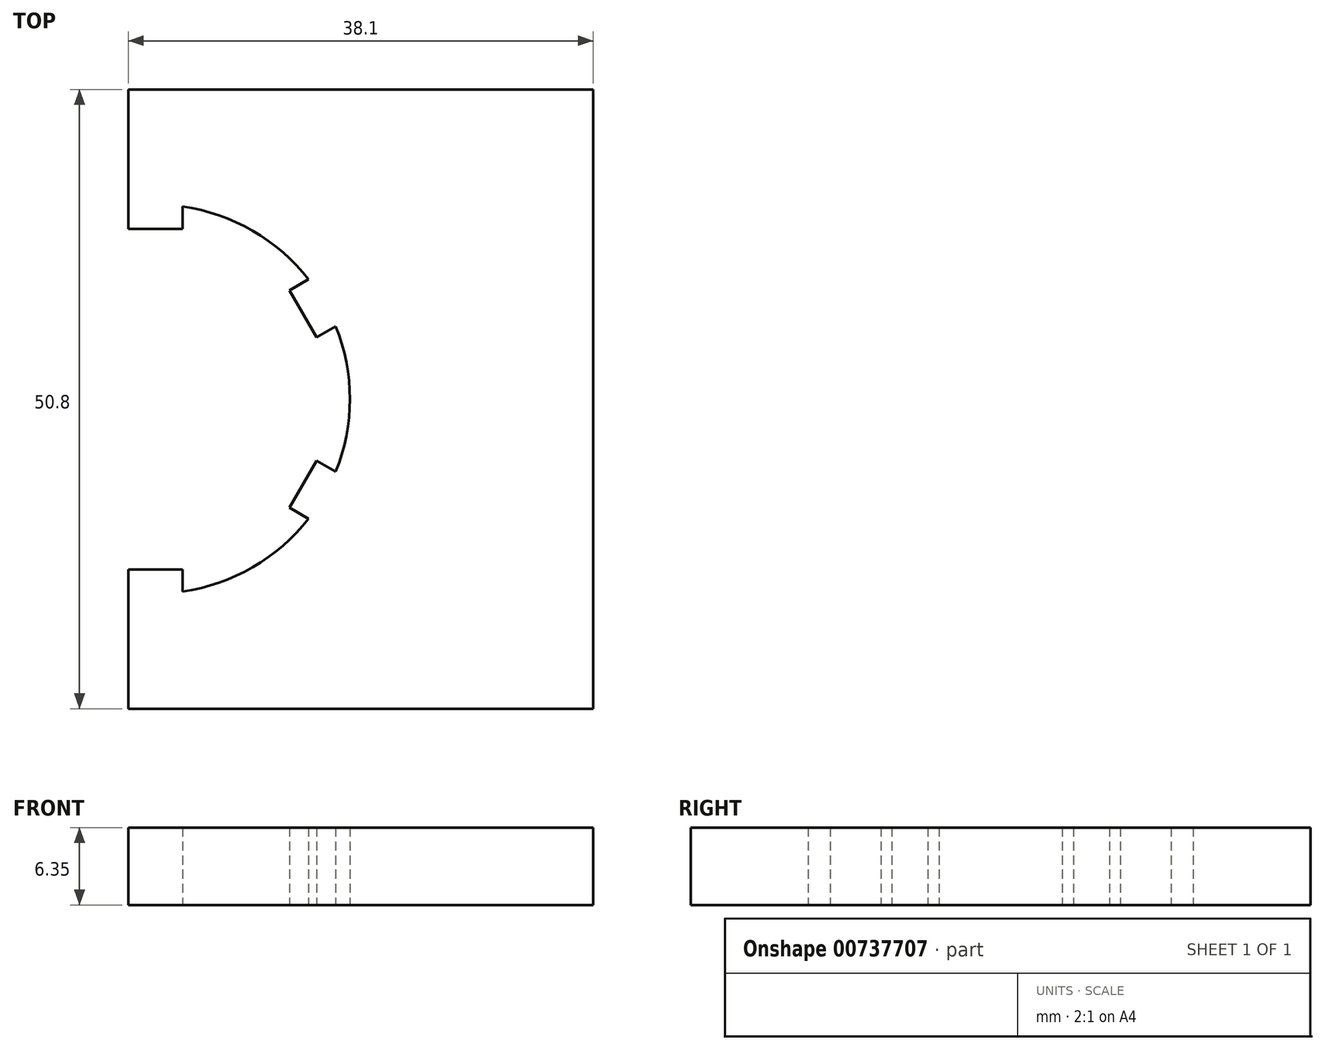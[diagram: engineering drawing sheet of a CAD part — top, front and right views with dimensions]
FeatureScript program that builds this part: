
annotation { "Feature Type Name" : "Feature", "Feature Type Description" : "" }
export const myFeature = defineFeature(function(context is Context, id is Id, definition is map)
    precondition{}
    {
        {
            var Q0;
            Q0=qCreatedBy(makeId("Top.planeOp"),FACE);
            var sketch = newSketch(context, id + "F0", { "sketchPlane" : qUnion([Q0])});
            skCircle(sketch, "E0", {"center": v(0, 0) * mm, "radius": 15.94 * mm, "construction": true});
            skLineSegment(sketch, "E1", {"start": v(0, 0) * mm, "end": v(0, 21.25) * mm});
            skLineSegment(sketch, "E2.0", {"start": v(2.22, 13.97) * mm, "end": v(2.22, 15.78) * mm, "construction": true});
            skLineSegment(sketch, "E3.0", {"start": v(-2.22, 13.97) * mm, "end": v(-2.22, 15.78) * mm, "construction": true});
            skLineSegment(sketch, "E4", {"start": v(-2.22, 13.97) * mm, "end": v(2.22, 13.97) * mm, "construction": true});
            skLineSegment(sketch, "E5", {"start": v(-20.95, 0) * mm, "end": v(26.76, 0) * mm, "construction": true});
            skPoint(sketch, "E6.orphan", {"position": v(-2.22, 0) * mm});
            skPoint(sketch, "E7.MirrorCS.end.orphan", {"position": v(2.22, 13.97) * mm});
            skPoint(sketch, "E7.MirrorCS.start.orphan", {"position": v(6.67, 13.97) * mm});
            skLineSegment(sketch, "E8.1.0", {"start": v(-13.2, 5.06) * mm, "end": v(-14.78, 5.97) * mm, "construction": true});
            skLineSegment(sketch, "E8.1.1", {"start": v(-13.2, 5.06) * mm, "end": v(-10.99, 8.9) * mm, "construction": true});
            skLineSegment(sketch, "E8.1.2", {"start": v(-10.99, 8.9) * mm, "end": v(-12.56, 9.82) * mm, "construction": true});
            skLineSegment(sketch, "E8.2.0", {"start": v(-10.99, -8.9) * mm, "end": v(-12.56, -9.82) * mm, "construction": true});
            skLineSegment(sketch, "E8.2.1", {"start": v(-10.99, -8.9) * mm, "end": v(-13.2, -5.06) * mm, "construction": true});
            skLineSegment(sketch, "E8.2.2", {"start": v(-13.2, -5.06) * mm, "end": v(-14.78, -5.97) * mm, "construction": true});
            skLineSegment(sketch, "E8.3.0", {"start": v(2.22, -13.97) * mm, "end": v(2.22, -15.78) * mm, "construction": true});
            skLineSegment(sketch, "E8.3.1", {"start": v(2.22, -13.97) * mm, "end": v(-2.22, -13.97) * mm, "construction": true});
            skLineSegment(sketch, "E8.3.2", {"start": v(-2.22, -13.97) * mm, "end": v(-2.22, -15.78) * mm, "construction": true});
            skLineSegment(sketch, "E8.4.0", {"start": v(13.2, -5.06) * mm, "end": v(14.78, -5.97) * mm, "construction": true});
            skLineSegment(sketch, "E8.4.1", {"start": v(13.2, -5.06) * mm, "end": v(10.99, -8.9) * mm, "construction": true});
            skLineSegment(sketch, "E8.4.2", {"start": v(10.99, -8.9) * mm, "end": v(12.56, -9.82) * mm, "construction": true});
            skLineSegment(sketch, "E8.5.0", {"start": v(10.99, 8.9) * mm, "end": v(12.56, 9.82) * mm, "construction": true});
            skLineSegment(sketch, "E8.5.1", {"start": v(10.99, 8.9) * mm, "end": v(13.2, 5.06) * mm, "construction": true});
            skLineSegment(sketch, "E8.5.2", {"start": v(13.2, 5.06) * mm, "end": v(14.78, 5.97) * mm, "construction": true});
            skSolve(sketch);
        }
        {
            var Q0;
            Q0=qCreatedBy(makeId("Top.planeOp"),FACE);
            var sketch = newSketch(context, id + "F1", { "sketchPlane" : qUnion([Q0])});
            skLineSegment(sketch, "E9.0", {"start": v(-2.22, 13.97) * mm, "end": v(2.22, 13.97) * mm});
            skLineSegment(sketch, "E10.0", {"start": v(2.22, 13.97) * mm, "end": v(2.22, 15.78) * mm});
            skLineSegment(sketch, "E11.0", {"start": v(-2.22, 13.97) * mm, "end": v(-2.22, 15.78) * mm});
            skPoint(sketch, "E12.0", {"position": v(11.77, 9.36) * mm});
            skLineSegment(sketch, "E13.0", {"start": v(10.99, 8.9) * mm, "end": v(12.56, 9.82) * mm});
            skLineSegment(sketch, "E14.0", {"start": v(10.99, 8.9) * mm, "end": v(13.2, 5.06) * mm});
            skLineSegment(sketch, "E15.0", {"start": v(13.2, 5.06) * mm, "end": v(14.78, 5.97) * mm});
            skLineSegment(sketch, "E16.0", {"start": v(13.2, -5.06) * mm, "end": v(10.99, -8.9) * mm});
            skLineSegment(sketch, "E17.0", {"start": v(13.2, -5.06) * mm, "end": v(14.78, -5.97) * mm});
            skLineSegment(sketch, "E18.0", {"start": v(10.99, -8.9) * mm, "end": v(12.56, -9.82) * mm});
            skLineSegment(sketch, "E19.0", {"start": v(2.22, -13.97) * mm, "end": v(-2.22, -13.97) * mm});
            skLineSegment(sketch, "E20.0", {"start": v(2.22, -13.97) * mm, "end": v(2.22, -15.78) * mm});
            skLineSegment(sketch, "E21.0", {"start": v(-2.22, -13.97) * mm, "end": v(-2.22, -15.78) * mm});
            skArc(sketch, "E22.0", {"start": v(2.22, -15.78) * mm, "mid": v(7.97, -13.8) * mm, "end": v(12.56, -9.82) * mm});
            skArc(sketch, "E23.trimOffspring", {"start": v(14.78, -5.97) * mm, "mid": v(15.94, 0) * mm, "end": v(14.78, 5.97) * mm});
            skArc(sketch, "E24.trimOffspring", {"start": v(12.56, 9.82) * mm, "mid": v(7.97, 13.8) * mm, "end": v(2.22, 15.78) * mm});
            skLineSegment(sketch, "E25", {"start": v(-2.22, -15.78) * mm, "end": v(-2.22, -25.4) * mm});
            skLineSegment(sketch, "E26", {"start": v(-2.22, -25.4) * mm, "end": v(35.88, -25.4) * mm});
            skLineSegment(sketch, "E27", {"start": v(35.88, -25.4) * mm, "end": v(35.88, 25.4) * mm});
            skLineSegment(sketch, "E28", {"start": v(-2.22, 15.78) * mm, "end": v(-2.22, 25.4) * mm});
            skLineSegment(sketch, "E29", {"start": v(-2.22, 25.4) * mm, "end": v(35.88, 25.4) * mm});
            skSolve(sketch);
        }
        {
            var Q0;
            Q0 = qSketchRegion(id + "F1", true);
            extrude(context, id + "F2", {"entities" : qUnion([Q0]), "depth" : 6.35 * mm, "offsetDistance" : 25.4 * mm});
        }
    });
